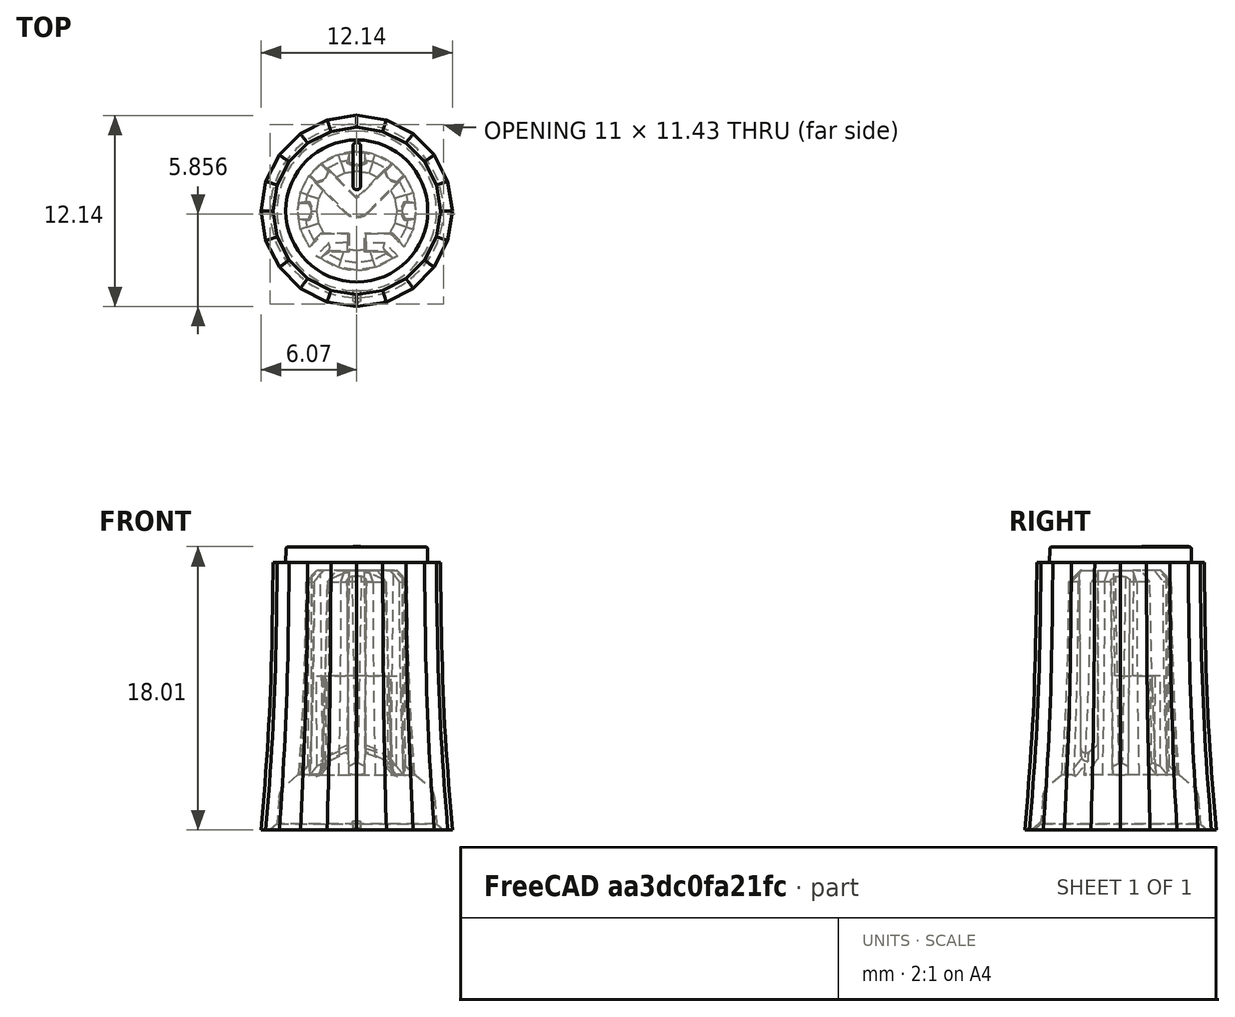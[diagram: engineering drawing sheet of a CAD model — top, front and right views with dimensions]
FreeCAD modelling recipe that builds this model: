
FCSTD DOCUMENT  (FreeCAD 1.0R39319 (Git))
Label: PLASTIC-KNOB-POT_v2
License: All rights reserved
LicenseURL: https://en.wikipedia.org/wiki/All_rights_reserved
objects: TechDraw::DrawHatch×14, TechDraw::DrawViewDimension×12, TechDraw::DrawViewBalloon×10, TechDraw::DrawViewPart×9, Sketcher::SketchObject×7, TechDraw::DrawViewAnnotation×3, PartDesign::Pad×3, Part::Feature×2, PartDesign::Boolean×2, TechDraw::DrawSVGTemplate×2, PartDesign::Body×2, TechDraw::DrawPage×2, PartDesign::Pocket×2, PartDesign::Plane×2, PartDesign::PolarPattern×2, PartDesign::Mirrored×1, PartDesign::CoordinateSystem×1, TechDraw::DrawComplexSection×1
note: 69 computed .brp shape members not serialized (recipe doc carries the construction recipe); baked Part::Feature solids carry a one-line shape summary decoded from their .brp

FEATURE [Part::Feature] Part__Feature  label="potmeter"
  shape: bbox 15.71 x 15.32 x 34.99 mm, 134 faces (baked)
FEATURE [PartDesign::Boolean] Boolean
  Group = -> [Part__Feature]
  Suppressed = false
  Type = 0
  UsePlacement = false
FEATURE [TechDraw::DrawSVGTemplate] Template
  EditableTexts = COLOR=Black - RAL code: 9004; CreationDate=2025-07-31; E.G.APPROVED=APPROVED; FC-Scale=5:1; FC-Title=PLASTIC - KNOB - POT; IntechStudioLtd.=Intech Studio Ltd.; MATERIAL=ABS - Terluran GP22; REV=03; STANDARD=DIN 16742-TG4
  Height = 297
  Orientation = 1
  Template = <userpath>/Documents/grid-hardware/Manufacturing/FreeCAD_technical_drawing_template/A3_LandscapeTD_MODIFIED.svg
  Width = 420
FEATURE [Sketcher::SketchObject] Sketch
  ArcFitTolerance = 0
  AttachmentSupport = -> [XZ_Plane]
  FullyConstrained = true
  MakeInternals = false
  MapMode = 5
  Placement = pos=(0,0,0) rot=(1,0,0;1.5708rad)
  sketch-geometry (1):
    g0: LineSegment StartX=0 StartY=19 StartZ=0 EndX=0 EndY=-1 EndZ=0
  constraints (4):
    c: PointOnObject(g0,g-2)
    c: Vertical(g0)
    c: DistanceY(g0,g0) = 20
    c: DistanceY(g0,g-1) = 1
FEATURE [TechDraw::DrawSVGTemplate] Template001
  EditableTexts = COLOR=White - RAL code: 9003; CreationDate=2024/01/02; E.G.APPROVED=APPROVED; FC-Scale=5:1; FC-Title=Potmeter knob painting; IntechStudioLtd.=Intech Studio Ltd.; MATERIAL=Tampo or screen printing; REV=02; STANDARD=N/A
  Height = 297
  Orientation = 1
  Template = <userpath>/Documents/grid-hardware/Manufacturing/FreeCAD_technical_drawing_template/A3_LandscapeTD_MODIFIED.svg
  Width = 420
FEATURE [TechDraw::DrawViewAnnotation] Annotation
  Font = osifont
  LineSpace = 100
  LockPosition = false
  MaxWidth = -1
  Rotation = 0
  ScaleType = 0
  Text = Painting material: | Resistance against scratches is critical to quality | Color: White - RAL code: 9003
  TextSize = 4
  TextStyle = 0
  X = 275.791
  Y = 85.9122
FEATURE [Part::Feature] Part__Feature001  label="potmeter001"
  shape: bbox 15.71 x 15.32 x 34.99 mm, 134 faces (baked)
FEATURE [PartDesign::Boolean] Boolean001
  Group = -> [Part__Feature001]
  Suppressed = false
  Type = 0
  UsePlacement = false
FEATURE [Sketcher::SketchObject] Sketch002
  ArcFitTolerance = 0
  AttachmentSupport = -> [XZ_Plane001]
  FullyConstrained = true
  MakeInternals = false
  MapMode = 5
  Placement = pos=(0,0,0) rot=(1,0,0;1.5708rad)
  sketch-geometry (1):
    g0: LineSegment StartX=0 StartY=19 StartZ=0 EndX=0 EndY=-1 EndZ=0
  constraints (4):
    c: PointOnObject(g0,g-2)
    c: Vertical(g0)
    c: DistanceY(g0,g0) = 20
    c: DistanceY(g0,g-1) = 1
FEATURE [Sketcher::SketchObject] Sketch003
  ArcFitTolerance = 0
  AttachmentSupport = -> [Boolean001]
  ExternalGeometry = -> [Boolean001]
  FullyConstrained = true
  MakeInternals = false
  MapMode = 5
  Placement = pos=(0,0,18) rot=(0,0,1;0rad)
  sketch-geometry (5):
    g0: ArcOfCircle CenterX=0 CenterY=1.6013 CenterZ=0 NormalX=0 NormalY=0 NormalZ=1 AngleXU=0 Radius=0.25 StartAngle=3.14159 EndAngle=6.28319
    g1: ArcOfCircle CenterX=0 CenterY=4.1013 CenterZ=0 NormalX=0 NormalY=0 NormalZ=1 AngleXU=0 Radius=0.25 StartAngle=1.728e-12 EndAngle=3.14159
    g2: LineSegment [constr] StartX=0 StartY=4.3513 StartZ=0 EndX=0 EndY=1.3513 EndZ=0
    g3: LineSegment StartX=-0.25 StartY=4.1013 StartZ=0 EndX=-0.25 EndY=1.6013 EndZ=0
    g4: LineSegment StartX=0.25 StartY=4.1013 StartZ=0 EndX=0.25 EndY=1.6013 EndZ=0
  constraints (14):
    c: PointOnObject(g0,g-2)
    c: PointOnObject(g1,g-2)
    c: Tangent(g1,g-3)
    c: PointOnObject(g2,g1)
    c: PointOnObject(g2,g0)
    c: Vertical(g2)
    c: Equal(g0,g1)
    c: Diameter(g1) = 0.5
    c: PointOnObject(g2,g-2)
    c: Tangent(g1,g4) = 1.5708
    c: Tangent(g1,g3) = -1.5708
    c: Tangent(g0,g3) = -1.5708
    c: Tangent(g0,g4) = 1.5708
    c: DistanceY(g2,g2) = 3
FEATURE [PartDesign::Pad] Pad  label="Paint"
  BaseFeature = -> Boolean001
  Direction = (0,0,1)
  Length = 0.01
  Length2 = 10
  Profile = -> Sketch003
  ReferenceAxis = -> Sketch003 [N_Axis]
  Suppressed = false
  Type = 0
FEATURE [PartDesign::Body] Body001  label="PLASTIC-KNOB_Painted"
  AllowCompound = false
  Group = -> [Boolean001,Sketch002,Sketch003,Pad]
  Origin = -> Origin001
  Tip = -> Pad
FEATURE [TechDraw::DrawViewPart] View005
  CoarseView = false
  Direction = (0,0,1)
  Focus = 100
  HardHidden = false
  IsoCount = 0
  IsoHidden = false
  IsoVisible = true
  LockPosition = false
  Perspective = false
  Rotation = 0
  Scale = 5
  ScaleType = 2
  ScrubCount = 0
  SeamHidden = false
  SeamVisible = true
  SmoothHidden = false
  SmoothVisible = true
  Source = -> [Pad]
  X = 97.3884
  XDirection = (1,0,0)
  Y = 204.513
FEATURE [TechDraw::DrawViewPart] View006
  CoarseView = false
  Direction = (-1,0,0)
  Focus = 100
  HardHidden = false
  IsoCount = 0
  IsoHidden = false
  IsoVisible = true
  LockPosition = false
  Perspective = false
  Rotation = 0
  Scale = 5
  ScaleType = 2
  ScrubCount = 0
  SeamHidden = false
  SeamVisible = true
  SmoothHidden = false
  SmoothVisible = true
  Source = -> [Pad]
  X = 207.371
  XDirection = (0,0,1)
  Y = 204.153
FEATURE [TechDraw::DrawViewPart] View007
  CoarseView = false
  Direction = (0.57735,0.57735,0.57735)
  Focus = 100
  HardHidden = false
  IsoCount = 0
  IsoHidden = false
  IsoVisible = true
  LockPosition = false
  Perspective = false
  Rotation = 0
  Scale = 5
  ScaleType = 2
  ScrubCount = 0
  SeamHidden = false
  SeamVisible = true
  SmoothHidden = false
  SmoothVisible = true
  Source = -> [Pad]
  X = 121.95
  XDirection = (-0.707107,0.707107,5.7735e-07)
  Y = 74.2227
FEATURE [TechDraw::DrawViewPart] View008
  CoarseView = false
  Direction = (0,0,-1)
  Focus = 100
  HardHidden = false
  IsoCount = 0
  IsoHidden = false
  IsoVisible = true
  LockPosition = false
  Perspective = false
  Rotation = 0
  Scale = 5
  ScaleType = 2
  ScrubCount = 0
  SeamHidden = false
  SeamVisible = true
  SmoothHidden = false
  SmoothVisible = true
  Source = -> [Pad]
  X = 327.125
  XDirection = (-1,0,0)
  Y = 202.189
FEATURE [TechDraw::DrawViewDimension] Dimension010
  AngleOverride = false
  Arbitrary = false
  ArbitraryTolerances = false
  EqualTolerance = true
  ExtensionAngle = 0
  FormatSpec = %.2w
  FormatSpecOverTolerance = %+.2w
  FormatSpecUnderTolerance = %+.2w
  Inverted = false
  LineAngle = 0
  LockPosition = false
  MeasureType = 1
  OverTolerance = 0
  References2D = -> [View005]
  Rotation = 0
  ScaleType = 0
  TheoreticalExact = false
  Type = 2
  UnderTolerance = 0
  X = -41.9183
  Y = 15.656
FEATURE [TechDraw::DrawViewDimension] Dimension011
  AngleOverride = false
  Arbitrary = false
  ArbitraryTolerances = false
  EqualTolerance = true
  ExtensionAngle = 0
  FormatSpec = %.2w
  FormatSpecOverTolerance = %+.2w
  FormatSpecUnderTolerance = %+.2w
  Inverted = false
  LineAngle = 0
  LockPosition = false
  MeasureType = 1
  OverTolerance = 0
  References2D = -> [View005]
  Rotation = 0
  ScaleType = 0
  TheoreticalExact = false
  Type = 1
  UnderTolerance = 0
  X = 34.5367
  Y = 20.8774
FEATURE [TechDraw::DrawHatch] Hatch009  label="Hatch009F17"
  HatchPattern = C:/Program Files/FreeCAD 0.21/data/Mod/TechDraw/Patterns/solid.svg
  Source = -> View007 [Face17,Face18,Face12,Face8,Face7,Face4,Face3,Face5,Face6,Face9,Face11,Face10,Face13,Face14,Face1]
FEATURE [TechDraw::DrawHatch] Hatch010  label="Hatch010F2"
  HatchPattern = C:/Program Files/FreeCAD 0.21/data/Mod/TechDraw/Patterns/solid.svg
  Source = -> View007 [Face2]
FEATURE [TechDraw::DrawViewBalloon] Balloon002
  BubbleShape = 1
  EndType = 0
  EndTypeScale = 1
  KinkLength = 0.1
  LockPosition = false
  OriginX = -4.24264
  OriginY = -4.24264
  Rotation = 0
  ScaleType = 0
  ShapeScale = 1
  SourceView = -> View008
  TextWrapLen = -1
  X = -5.3055
  Y = -10.5429
FEATURE [TechDraw::DrawViewAnnotation] Annotation001
  Font = osifont
  LineSpace = 100
  LockPosition = false
  MaxWidth = -1
  Rotation = 0
  ScaleType = 0
  Text = AESTHETICAL SURFACES: | COLORED BLUE ON THE ISOMETRIC VIEWS: SPI - D2 | NO BURRS, NO PARTING LINES, | NO EJECTION MARKS | FREE OF ANY DEFECTS | FREE OF ANY WELD OR MELD LINES | NON VISIBLE GATE LOCATION ALLOWED | REMAINING BLACK SURFACES: SPI - B2
  TextSize = 3
  TextStyle = 0
  X = 264.167
  Y = 100.12
FEATURE [TechDraw::DrawViewDimension] Dimension012
  AngleOverride = false
  Arbitrary = false
  ArbitraryTolerances = false
  EqualTolerance = true
  ExtensionAngle = 0
  FormatSpec = (%.2w)
  FormatSpecOverTolerance = %+.2w
  FormatSpecUnderTolerance = %+.2w
  Inverted = false
  LineAngle = 0
  LockPosition = false
  MeasureType = 1
  OverTolerance = 0
  References2D = -> [View005]
  Rotation = 0
  ScaleType = 0
  TheoreticalExact = false
  Type = 2
  UnderTolerance = 0
  X = -37.4834
  Y = -5.49655
FEATURE [TechDraw::DrawViewBalloon] Balloon003
  BubbleShape = 1
  EndType = 0
  EndTypeScale = 1
  KinkLength = -0.1
  LockPosition = false
  OriginX = 1.59e-14
  OriginY = 1.3513
  Rotation = 0
  ScaleType = 0
  ShapeScale = 1
  SourceView = -> View005
  Text = Orientation of the painted line relative to inner geometry is critical to quality
  TextWrapLen = -1
  X = 24.0964
  Y = -11.4876
FEATURE [TechDraw::DrawViewBalloon] Balloon004
  BubbleShape = 2
  EndType = 6
  EndTypeScale = 1
  KinkLength = 0
  LockPosition = false
  OriginX = -50.6224
  OriginY = 14.8162
  Rotation = 0
  ScaleType = 0
  ShapeScale = 1
  SourceView = -> Dimension010
  Text = 2
  TextWrapLen = -1
  X = -51.7505
  Y = 12.4076
FEATURE [TechDraw::DrawViewBalloon] Balloon005
  BubbleShape = 2
  EndType = 0
  EndTypeScale = 1
  KinkLength = 0
  LockPosition = false
  OriginX = 35.0518
  OriginY = 20.0598
  Rotation = 0
  ScaleType = 0
  ShapeScale = 1
  SourceView = -> Dimension011
  Text = 2
  TextWrapLen = -1
  X = 45.9782
  Y = 13.5369
FEATURE [TechDraw::DrawPage] Page001  label="PLASTIC-KNOB-POT_Painting_drawing"
  KeepUpdated = true
  NextBalloonIndex = 9
  ProjectionType = 0
  Template = -> Template001
  Views = -> [Annotation,View005,View006,View007,View008,Dimension010,Dimension011,Balloon002,Dimension012,Balloon003,Balloon004,Balloon005]
FEATURE [TechDraw::DrawViewAnnotation] Annotation002
  Font = osifont
  LineSpace = 100
  LockPosition = false
  MaxWidth = -1
  Rotation = 0
  ScaleType = 0
  Text = Section A-A
  TextSize = 4
  TextStyle = 0
  X = 193.37
  Y = 128.632
FEATURE [Sketcher::SketchObject] Sketch008
  ArcFitTolerance = 0
  AttachmentSupport = -> [XY_Plane]
  FullyConstrained = true
  MakeInternals = false
  MapMode = 5
  sketch-geometry (6):
    g0: ArcOfCircle CenterX=0 CenterY=0 CenterZ=0 NormalX=0 NormalY=0 NormalZ=1 AngleXU=0 Radius=2.95 StartAngle=0.615084 EndAngle=0.955712
    g1: LineSegment StartX=2.40934 StartY=1.70223 StartZ=0 EndX=2.05578 EndY=1.34868 EndZ=0
    g2: LineSegment StartX=2.05578 StartY=1.34868 StartZ=0 EndX=1.34868 EndY=2.05578 EndZ=0
    g3: LineSegment StartX=1.34868 StartY=2.05578 StartZ=0 EndX=1.70223 EndY=2.40934 EndZ=0
    g4: LineSegment [constr] StartX=2.08597 StartY=2.08597 StartZ=0 EndX=0 EndY=0 EndZ=0
    g5: GeomPoint [constr] X=1.70223 Y=1.70223 Z=0
  constraints (16):
    c: Coincident(g0,g-1)
    c: Diameter(g0) = 5.9
    c: Coincident(g2,g1)
    c: Coincident(g3,g2)
    c: PointOnObject(g4,g0)
    c: Coincident(g4,g0)
    c: Angle(g4,g-2) = 0.785398
    c: Parallel(g1,g4)
    c: Parallel(g4,g3)
    c: Perpendicular(g1,g2)
    c: Symmetric(g1,g2,g5)
    c: PointOnObject(g5,g4)
    c: Distance(g2) = 1
    c: Distance(g3) = 0.5
    c: Coincident(g0,g3)
    c: Coincident(g0,g1)
FEATURE [PartDesign::Pocket] Pocket
  BaseFeature = -> Boolean
  Direction = (0,0,-1)
  Length = 9.8
  Length2 = 5
  Profile = -> Sketch008
  ReferenceAxis = -> Sketch008 [N_Axis]
  Refine = true
  Reversed = true
  Suppressed = false
  Type = 0
FEATURE [PartDesign::Mirrored] Mirrored
  BaseFeature = -> Pocket
  MirrorPlane = -> Sketch008 [V_Axis]
  Originals = -> [Pocket]
  Refine = true
  Suppressed = false
  TransformMode = 0
FEATURE [Sketcher::SketchObject] Sketch009
  ArcFitTolerance = 0
  AttachmentSupport = -> [XY_Plane]
  FullyConstrained = true
  MakeInternals = false
  MapMode = 5
  sketch-geometry (5):
    g0: ArcOfCircle CenterX=0 CenterY=0 CenterZ=0 NormalX=0 NormalY=0 NormalZ=1 AngleXU=0 Radius=2.95 StartAngle=6.11287 EndAngle=6.4535
    g1: LineSegment StartX=2.90732 StartY=0.5 StartZ=0 EndX=2.40732 EndY=0.5 EndZ=0
    g2: LineSegment StartX=2.40732 StartY=0.5 StartZ=0 EndX=2.40732 EndY=-0.5 EndZ=0
    g3: LineSegment StartX=2.40732 StartY=-0.5 StartZ=0 EndX=2.90732 EndY=-0.5 EndZ=0
    g4: GeomPoint [constr] X=2.40732 Y=0 Z=0
  constraints (13):
    c: Coincident(g0,g-1)
    c: Diameter(g0) = 5.9
    c: Horizontal(g1)
    c: Coincident(g2,g1)
    c: Vertical(g2)
    c: Horizontal(g3)
    c: Coincident(g2,g3)
    c: Symmetric(g1,g2,g4)
    c: PointOnObject(g4,g-1)
    c: DistanceX(g1,g1) = 0.5
    c: DistanceY(g2,g2) = 1
    c: Coincident(g0,g1)
    c: Coincident(g0,g3)
FEATURE [PartDesign::Pocket] Pocket001
  BaseFeature = -> Mirrored
  Direction = (0,0,-1)
  Length = 16.5
  Length2 = 5
  Profile = -> Sketch009
  ReferenceAxis = -> Sketch009 [N_Axis]
  Refine = true
  Reversed = true
  Suppressed = false
  Type = 0
FEATURE [PartDesign::Plane] DatumPlane
  AttachmentOffset = pos=(0,0,0) rot=(0,-1,0;0.15708rad)
  AttachmentSupport = -> [XZ_Plane]
  Length = 67.9025
  MapMode = 5
  Placement = pos=(0,0,0) rot=(0.993863,-0.078219,-0.078219;1.57695rad)
  ResizeMode = 0
  Width = 60.6964
FEATURE [Sketcher::SketchObject] Sketch010
  ArcFitTolerance = 0
  AttachmentSupport = -> [DatumPlane]
  FullyConstrained = true
  MakeInternals = false
  MapMode = 5
  Placement = pos=(0,0,0) rot=(0.993863,-0.078219,-0.078219;1.57695rad)
  sketch-geometry (3):
    g0: LineSegment StartX=2.50536 StartY=16.5 StartZ=0 EndX=3.50536 EndY=15.4768 EndZ=0
    g1: LineSegment StartX=2.50536 StartY=16.5 StartZ=0 EndX=3.50536 EndY=16.5 EndZ=0
    g2: LineSegment StartX=3.50536 StartY=16.5 StartZ=0 EndX=3.50536 EndY=15.4768 EndZ=0
  constraints (9):
    c: DistanceY(g-1,g0) = 16.5
    c: DistanceX(g-1,g0) = 2.50536
    c: DistanceX(g0,g0) = 1
    c: Coincident(g1,g0)
    c: Coincident(g2,g1)
    c: Coincident(g2,g0)
    c: Horizontal(g1)
    c: Vertical(g2)
    c: Angle(g0,g1) = 0.796848
FEATURE [PartDesign::PolarPattern] PolarPattern
  Angle = 180
  Axis = -> Sketch009 [N_Axis]
  BaseFeature = -> Pocket001
  Mode = 0
  Occurrences = 3
  Offset = 120
  Originals = -> [Pocket001]
  Refine = true
  Suppressed = false
  TransformMode = 0
FEATURE [PartDesign::Pad] Pad001
  BaseFeature = -> PolarPattern
  Direction = (-0.156434,-0.987688,0)
  Length = 2
  Length2 = 10
  Midplane = true
  Profile = -> Sketch010
  ReferenceAxis = -> Sketch010 [N_Axis]
  Suppressed = false
  Type = 0
FEATURE [PartDesign::Plane] DatumPlane001
  AttachmentOffset = pos=(0,0,0) rot=(0,1,0;0.15708rad)
  AttachmentSupport = -> [XZ_Plane]
  Length = 67.9025
  MapMode = 5
  Placement = pos=(0,0,0) rot=(0.993863,0.078219,0.078219;1.57695rad)
  ResizeMode = 0
  Width = 60.6964
FEATURE [Sketcher::SketchObject] Sketch011
  ArcFitTolerance = 0
  AttachmentSupport = -> [DatumPlane001]
  FullyConstrained = true
  MakeInternals = false
  MapMode = 5
  Placement = pos=(0,0,0) rot=(0.993863,0.078219,0.078219;1.57695rad)
  sketch-geometry (3):
    g0: LineSegment StartX=2.50536 StartY=16.5 StartZ=0 EndX=3.50536 EndY=15.4768 EndZ=0
    g1: LineSegment StartX=3.50536 StartY=15.4768 StartZ=0 EndX=3.50536 EndY=16.5 EndZ=0
    g2: LineSegment StartX=3.50536 StartY=16.5 StartZ=0 EndX=2.50536 EndY=16.5 EndZ=0
  constraints (9):
    c: Coincident(g1,g0)
    c: Vertical(g1)
    c: Coincident(g2,g1)
    c: Coincident(g2,g0)
    c: Horizontal(g2)
    c: DistanceX(g0,g0) = 1
    c: DistanceY(g-1,g0) = 16.5
    c: DistanceX(g-1,g0) = 2.50536
    c: Angle(g0,g2) = 0.796848
FEATURE [PartDesign::Pad] Pad002
  BaseFeature = -> Pad001
  Direction = (0.156434,-0.987688,0)
  Length = 2
  Length2 = 10
  Midplane = true
  Profile = -> Sketch011
  ReferenceAxis = -> Sketch011 [N_Axis]
  Suppressed = false
  Type = 0
FEATURE [PartDesign::PolarPattern] PolarPattern001
  Angle = 180
  Axis = -> Z_Axis
  BaseFeature = -> Pad002
  Mode = 0
  Occurrences = 3
  Offset = 120
  Originals = -> [Pad001,Pad002]
  Suppressed = false
  TransformMode = 0
FEATURE [TechDraw::DrawViewBalloon] Balloon007
  BubbleShape = 2
  EndType = 0
  EndTypeScale = 1
  KinkLength = 5
  LockPosition = false
  OriginX = 12.601
  OriginY = 50.5283
  Rotation = 0
  ScaleType = 0
  ShapeScale = 1
  Text = 3
  TextWrapLen = -1
  X = 32.2609
  Y = 41.9645
FEATURE [TechDraw::DrawViewBalloon] Balloon008
  BubbleShape = 2
  EndType = 0
  EndTypeScale = 1
  KinkLength = 5
  LockPosition = false
  OriginX = 44.2251
  OriginY = 14.1435
  Rotation = 0
  ScaleType = 0
  ShapeScale = 1
  Text = 3
  TextWrapLen = -1
  X = 50.2833
  Y = -19.9235
FEATURE [PartDesign::CoordinateSystem] LCS_1
  AttacherType = Attacher::AttachEngine3D
  AttachmentSupport = -> [PolarPattern001]
  MapMode = 5
  Placement = pos=(0,0,9.8) rot=(1,0,0;3.14159rad)
FEATURE [PartDesign::Body] Body  label="PLASTIC-KNOB-POT_v2"
  AllowCompound = false
  Group = -> [Boolean,Sketch,Sketch008,Pocket,Mirrored,Sketch009,Pocket001,DatumPlane,Sketch010,PolarPattern,Pad001,DatumPlane001,Sketch011,Pad002,PolarPattern001,LCS_1]
  Origin = -> Origin
  Tip = -> PolarPattern001
FEATURE [TechDraw::DrawViewPart] View
  CoarseView = false
  Direction = (0,-1,0)
  Focus = 100
  HardHidden = false
  IsoCount = 0
  IsoHidden = false
  IsoVisible = true
  LockPosition = false
  Perspective = false
  Rotation = 0
  Scale = 5
  ScaleType = 2
  ScrubCount = 0
  SeamHidden = false
  SeamVisible = true
  SmoothHidden = false
  SmoothVisible = true
  Source = -> [Body]
  X = 98.421
  XDirection = (1,0,-1e-06)
  Y = 192.804
FEATURE [TechDraw::DrawComplexSection] ComplexSection  label="Section A - A"
  BaseView = -> View
  CoarseView = false
  CutSurfaceDisplay = 2
  CuttingToolWireObject = -> Sketch
  Direction = (-1,0,1e-06)
  FileGeomPattern = C:/Program Files/FreeCAD 0.21/data/Mod/TechDraw/PAT/FCPAT.pat
  FileHatchPattern = C:/Program Files/FreeCAD 0.21/data/Mod/TechDraw/Patterns/simple.svg
  Focus = 100
  FuseBeforeCut = false
  HardHidden = false
  HatchOffset = (0,0,0)
  HatchRotation = 0
  HatchScale = 1
  IsoCount = 0
  IsoHidden = false
  IsoVisible = false
  LockPosition = false
  NameGeomPattern = Gyémánt bevonatú
  Perspective = false
  ProjectionStrategy = 0
  Rotation = -90
  Scale = 5
  ScaleType = 2
  ScrubCount = 0
  SeamHidden = false
  SeamVisible = true
  SectionDirection = 4
  SectionLineStretch = 1
  SectionNormal = (-1,0,1e-06)
  SectionOrigin = (0,0,0)
  SectionSymbol = A
  SmoothHidden = false
  SmoothVisible = true
  Source = -> [Body]
  TrimAfterCut = false
  UsePreviousCut = false
  X = 193.568
  XDirection = (-1e-06,0,-1)
  Y = 192.821
FEATURE [TechDraw::DrawViewPart] View003
  CoarseView = false
  Direction = (-0.57735,-0.57735,0.57735)
  Focus = 100
  HardHidden = false
  IsoCount = 0
  IsoHidden = false
  IsoVisible = true
  LockPosition = false
  Perspective = false
  Rotation = 0
  Scale = 2
  ScaleType = 2
  ScrubCount = 0
  SeamHidden = false
  SeamVisible = true
  SmoothHidden = false
  SmoothVisible = true
  Source = -> [Body]
  X = 379.046
  XDirection = (0.707107,-0.707107,0)
  Y = 107.401
FEATURE [TechDraw::DrawViewPart] View004
  CoarseView = false
  Direction = (-0.57735,-0.57735,-0.57735)
  Focus = 100
  HardHidden = false
  IsoCount = 0
  IsoHidden = false
  IsoVisible = true
  LockPosition = false
  Perspective = false
  Rotation = 0
  Scale = 2
  ScaleType = 2
  ScrubCount = 0
  SeamHidden = false
  SeamVisible = true
  SmoothHidden = false
  SmoothVisible = true
  Source = -> [Body]
  X = 337.082
  XDirection = (0.707106,-0.707106,0)
  Y = 107.401
FEATURE [TechDraw::DrawHatch] Hatch001  label="Hatch001F2"
  HatchPattern = C:/Program Files/FreeCAD 0.21/data/Mod/TechDraw/Patterns/solid.svg
  Source = -> View003 [Face2,Face13,Face4,Face5,Face3,Face6,Face9,Face8,Face7,Face12,Face11,Face10]
FEATURE [TechDraw::DrawHatch] Hatch002  label="Hatch002F1"
  HatchPattern = C:/Program Files/FreeCAD 0.21/data/Mod/TechDraw/Patterns/solid.svg
  Source = -> View003 [Face1]
FEATURE [TechDraw::DrawViewBalloon] Balloon
  BubbleShape = 1
  EndType = 3
  EndTypeScale = 1
  KinkLength = 0
  LockPosition = false
  OriginX = -2.29422
  OriginY = 3.04373
  Rotation = 0
  ScaleType = 0
  ShapeScale = 1
  SourceView = -> View004
  TextWrapLen = -1
  X = -16.2526
  Y = -5.35905
FEATURE [TechDraw::DrawViewPart] View002
  CoarseView = false
  Direction = (1e-06,0,1)
  Focus = 100
  HardHidden = false
  IsoCount = 0
  IsoHidden = false
  IsoVisible = true
  LockPosition = false
  Perspective = false
  Rotation = 0
  Scale = 5
  ScaleType = 2
  ScrubCount = 0
  SeamHidden = false
  SeamVisible = true
  SmoothHidden = false
  SmoothVisible = true
  Source = -> [Body]
  X = 100.462
  XDirection = (1,0,-1e-06)
  Y = 74.8021
FEATURE [TechDraw::DrawViewDimension] Dimension009
  AngleOverride = false
  Arbitrary = false
  ArbitraryTolerances = false
  EqualTolerance = true
  ExtensionAngle = 0
  FormatSpec = 10× %.2w
  FormatSpecOverTolerance = %+.2w
  FormatSpecUnderTolerance = %+.2w
  Inverted = false
  LineAngle = 0
  LockPosition = false
  MeasureType = 1
  OverTolerance = 0
  References2D = -> [View002]
  Rotation = 0
  ScaleType = 0
  TheoreticalExact = false
  Type = 0
  UnderTolerance = 0
  X = -39.2324
  Y = 9.93901
FEATURE [TechDraw::DrawViewDimension] Dimension013
  AngleOverride = false
  Arbitrary = false
  ArbitraryTolerances = false
  EqualTolerance = true
  ExtensionAngle = 0
  FormatSpec = ⌀%.2w
  FormatSpecOverTolerance = %+.2w
  FormatSpecUnderTolerance = %+.2w
  Inverted = false
  LineAngle = 0
  LockPosition = false
  MeasureType = 1
  OverTolerance = 0
  References2D = -> [View]
  Rotation = 0
  ScaleType = 0
  TheoreticalExact = false
  Type = 1
  UnderTolerance = 0
  X = -8.9e-05
  Y = 66.4443
FEATURE [TechDraw::DrawViewDimension] Dimension014
  AngleOverride = false
  Arbitrary = false
  ArbitraryTolerances = false
  EqualTolerance = true
  ExtensionAngle = 0
  FormatSpec = %.2w
  FormatSpecOverTolerance = %+.2w
  FormatSpecUnderTolerance = %+.2w
  Inverted = false
  LineAngle = 0
  LockPosition = false
  MeasureType = 1
  OverTolerance = 0
  References2D = -> [View]
  Rotation = 0
  ScaleType = 0
  TheoreticalExact = false
  Type = 2
  UnderTolerance = 0
  X = 38.805
  Y = 45.2486
FEATURE [TechDraw::DrawViewDimension] Dimension015
  AngleOverride = false
  Arbitrary = false
  ArbitraryTolerances = false
  EqualTolerance = true
  ExtensionAngle = 0
  FormatSpec = %.2w
  FormatSpecOverTolerance = %+.2w
  FormatSpecUnderTolerance = %+.2w
  Inverted = false
  LineAngle = 0
  LockPosition = false
  MeasureType = 1
  OverTolerance = 0
  References2D = -> [View]
  Rotation = 0
  ScaleType = 0
  TheoreticalExact = false
  Type = 2
  UnderTolerance = 0
  X = -48.6863
  Y = 2.49998
FEATURE [TechDraw::DrawViewPart] View001
  CoarseView = false
  Direction = (-1e-06,0,-1)
  Focus = 100
  HardHidden = false
  IsoCount = 0
  IsoHidden = false
  IsoVisible = true
  LockPosition = false
  Perspective = false
  Rotation = 0
  Scale = 5
  ScaleType = 2
  ScrubCount = 0
  SeamHidden = false
  SeamVisible = true
  SmoothHidden = false
  SmoothVisible = true
  Source = -> [Body]
  X = 305.681
  XDirection = (1,0,-1e-06)
  Y = 190.563
FEATURE [TechDraw::DrawViewDimension] Dimension017
  AngleOverride = false
  Arbitrary = false
  ArbitraryTolerances = false
  BoxCorners = (2) [(-30.374,-30.374,-1e-07),(30.374,30.374,1e-07)]
  EqualTolerance = true
  ExtensionAngle = 0
  FormatSpec = ⌀%.2w
  FormatSpecOverTolerance = %+.2w
  FormatSpecUnderTolerance = %+.2w
  Inverted = false
  LineAngle = 0
  LockPosition = false
  MeasureType = 1
  OverTolerance = 0
  References2D = -> [View001]
  Rotation = 0
  ScaleType = 0
  TheoreticalExact = false
  Type = 5
  UnderTolerance = 0
  X = -43.4
  Y = 27.6231
FEATURE [TechDraw::DrawViewDimension] Dimension
  AngleOverride = false
  Arbitrary = false
  ArbitraryTolerances = false
  BoxCorners = (2) [(-30.374,-45,-1e-07),(30.374,45,1e-07)]
  EqualTolerance = true
  ExtensionAngle = 0
  FormatSpec = %.2w
  FormatSpecOverTolerance = %+.2w
  FormatSpecUnderTolerance = %+.2w
  Inverted = false
  LineAngle = 0
  LockPosition = false
  MeasureType = 1
  OverTolerance = 0.1
  References2D = -> [ComplexSection]
  Rotation = 0
  ScaleType = 0
  TheoreticalExact = false
  Type = 2
  UnderTolerance = -0.1
  X = 31.0773
  Y = -20.5
FEATURE [TechDraw::DrawViewDimension] Dimension021
  AngleOverride = false
  Arbitrary = false
  ArbitraryTolerances = false
  BoxCorners = (2) [(-30.374,-45,-1e-07),(30.374,45,1e-07)]
  EqualTolerance = false
  ExtensionAngle = 0
  FormatSpec = ⌀%.2w
  FormatSpecOverTolerance = %+.2w
  FormatSpecUnderTolerance = %+.2w
  Inverted = false
  LineAngle = 0
  LockPosition = false
  MeasureType = 1
  OverTolerance = 0.1
  References2D = -> [ComplexSection]
  Rotation = 0
  ScaleType = 0
  TheoreticalExact = false
  Type = 1
  UnderTolerance = 0
  X = -0.045274
  Y = -42.8297
FEATURE [TechDraw::DrawViewDimension] Dimension022
  AngleOverride = false
  Arbitrary = false
  ArbitraryTolerances = false
  BoxCorners = (2) [(-30.374,-30.374,-1e-07),(30.374,30.374,1e-07)]
  EqualTolerance = true
  ExtensionAngle = 0
  FormatSpec = %.2w
  FormatSpecOverTolerance = %+.2w
  FormatSpecUnderTolerance = %+.2w
  Inverted = false
  LineAngle = 0
  LockPosition = false
  MeasureType = 1
  OverTolerance = 0.05
  References2D = -> [View001]
  Rotation = 0
  ScaleType = 0
  TheoreticalExact = false
  Type = 1
  UnderTolerance = -0.05
  X = -5.1e-05
  Y = 54.1432
FEATURE [TechDraw::DrawViewDimension] Dimension023
  AngleOverride = false
  Arbitrary = false
  ArbitraryTolerances = false
  BoxCorners = (2) [(-30.374,-30.374,-1e-07),(30.374,30.374,1e-07)]
  EqualTolerance = true
  ExtensionAngle = 0
  FormatSpec = %.2w
  FormatSpecOverTolerance = %+.2w
  FormatSpecUnderTolerance = %+.2w
  Inverted = false
  LineAngle = 0
  LockPosition = false
  MeasureType = 1
  OverTolerance = 0.05
  References2D = -> [View001]
  Rotation = 0
  ScaleType = 0
  TheoreticalExact = false
  Type = 2
  UnderTolerance = -0.05
  X = 37.6716
  Y = 24.7624
FEATURE [TechDraw::DrawHatch] Hatch
  HatchPattern = /app/share/Mod/TechDraw/Patterns/solid.svg
  Source = -> View005 [Face4]
FEATURE [TechDraw::DrawHatch] Hatch011
  HatchPattern = /app/share/Mod/TechDraw/Patterns/solid.svg
  Source = -> View005 [Face6]
FEATURE [TechDraw::DrawViewBalloon] Balloon009
  BubbleShape = 2
  EndType = 0
  EndTypeScale = 1
  KinkLength = 5
  LockPosition = false
  OriginX = -5.92613
  OriginY = 0.938607
  Rotation = 0
  ScaleType = 0
  ShapeScale = 1
  SourceView = -> View001
  Text = 3
  TextWrapLen = -1
  X = -11.2478
  Y = 3.14051
FEATURE [TechDraw::DrawViewBalloon] Balloon010
  BubbleShape = 2
  EndType = 0
  EndTypeScale = 1
  KinkLength = 5
  LockPosition = false
  OriginX = -1.98815
  OriginY = 12.4234
  Rotation = 0
  ScaleType = 0
  ShapeScale = 1
  SourceView = -> View001
  Text = 3
  TextWrapLen = -1
  X = -5.51177
  Y = 10.7925
FEATURE [TechDraw::DrawViewBalloon] Balloon011
  BubbleShape = 2
  EndType = 0
  EndTypeScale = 1
  KinkLength = 5
  LockPosition = false
  OriginX = 11.1664
  OriginY = -5.13173
  Rotation = 0
  ScaleType = 0
  ShapeScale = 1
  SourceView = -> View001
  Text = 3
  TextWrapLen = -1
  X = 11.5702
  Y = 3.12692
FEATURE [TechDraw::DrawPage] Page  label="PLASTIC-KNOB-POT_Drawing"
  KeepUpdated = true
  NextBalloonIndex = 11
  ProjectionType = 0
  Template = -> Template
  Views = -> [View,View001,View002,ComplexSection,Dimension009,View003,View004,Annotation001,Balloon,Annotation002,Dimension013,Dimension014,Dimension015,Dimension017,Balloon007,Balloon008,Dimension,Dimension021,Dimension022,Dimension023,Balloon009,Balloon010,Balloon011]
FEATURE [TechDraw::DrawHatch] Hatch012
  HatchPattern = /app/share/Mod/TechDraw/Patterns/solid.svg
  Source = -> View004 [Face12,Face7,Face4,Face3,Face5,Face6,Face9]
FEATURE [TechDraw::DrawHatch] Hatch013
  HatchPattern = /app/share/Mod/TechDraw/Patterns/solid.svg
  Source = -> View004 [Face1,Face2,Face15,Face18,Face16,Face19]
FEATURE [TechDraw::DrawHatch] Hatch014
  HatchPattern = /app/share/Mod/TechDraw/Patterns/solid.svg
  Source = -> View004 [Face20,Face21,Face29,Face26,Face24,Face22,Face23,Face27,Face28]
FEATURE [TechDraw::DrawHatch] Hatch015
  HatchPattern = /app/share/Mod/TechDraw/Patterns/solid.svg
  Source = -> View004 [Face11,Face8,Face17]
FEATURE [TechDraw::DrawHatch] Hatch016
  HatchPattern = /app/share/Mod/TechDraw/Patterns/solid.svg
  Source = -> View004 [Face14]
FEATURE [TechDraw::DrawHatch] Hatch017
  HatchPattern = /app/share/Mod/TechDraw/Patterns/solid.svg
  Source = -> View004 [Face10]
FEATURE [TechDraw::DrawHatch] Hatch018
  HatchPattern = /app/share/Mod/TechDraw/Patterns/solid.svg
  Source = -> View004 [Face13]
FEATURE [TechDraw::DrawHatch] Hatch019
  HatchPattern = /app/share/Mod/TechDraw/Patterns/solid.svg
  Source = -> View004 [Face25,Face30]
